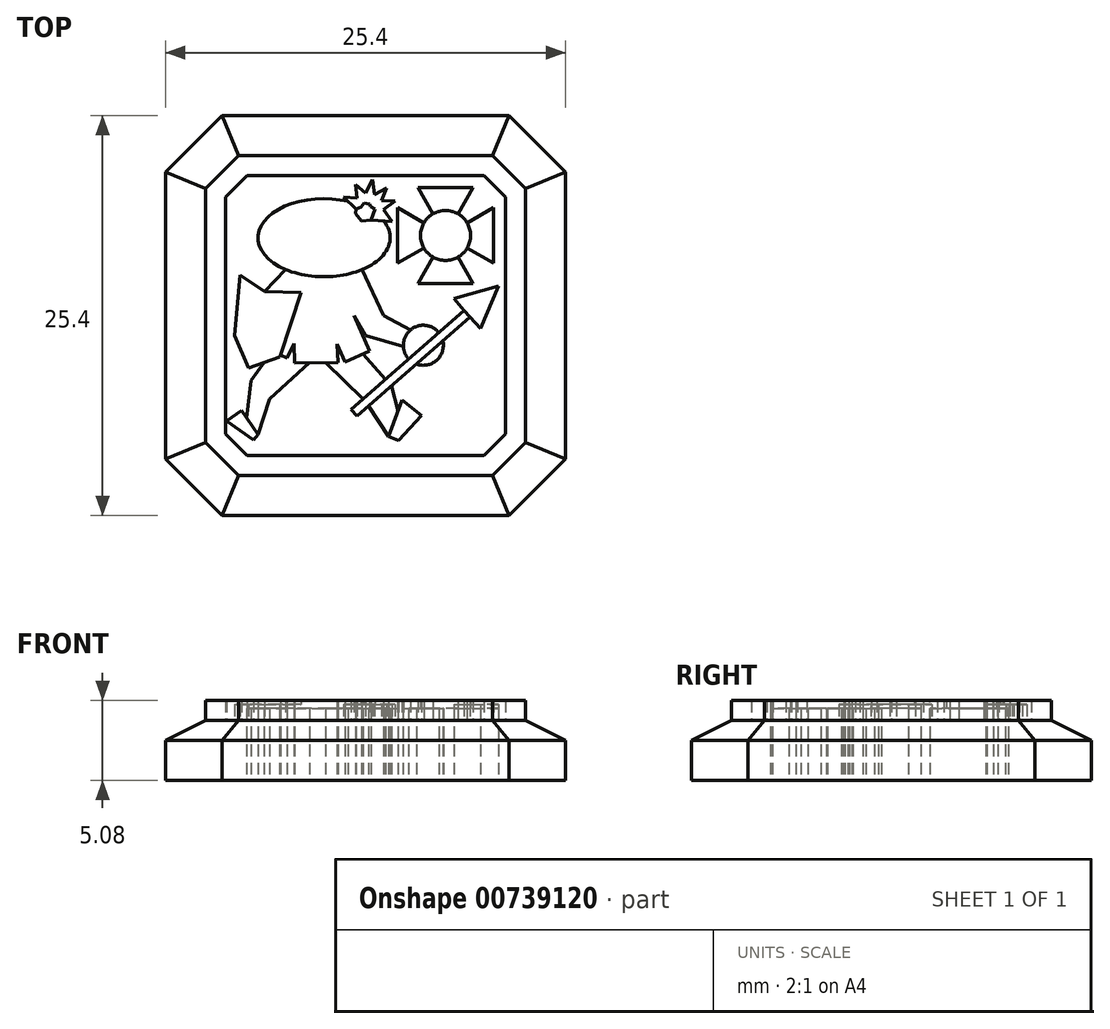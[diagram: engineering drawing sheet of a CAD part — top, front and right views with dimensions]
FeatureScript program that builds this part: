
annotation { "Feature Type Name" : "Feature", "Feature Type Description" : "" }
export const myFeature = defineFeature(function(context is Context, id is Id, definition is map)
    precondition{}
    {
        {
            var Q0;
            Q0=qCreatedBy(makeId("Top.planeOp"),FACE);
            var sketch = newSketch(context, id + "F0", { "sketchPlane" : qUnion([Q0])});
            skLineSegment(sketch, "E0", {"start": v(0, 34.78) * mm, "end": v(0, -32.67) * mm, "construction": true});
            skLineSegment(sketch, "E1", {"start": v(-47.17, 0) * mm, "end": v(41.3, 0) * mm});
            skLineSegment(sketch, "E2", {"start": v(0, 12.7) * mm, "end": v(-9.1, 12.7) * mm});
            skLineSegment(sketch, "E3", {"start": v(-9.1, 12.7) * mm, "end": v(-12.7, 9.1) * mm});
            skLineSegment(sketch, "E4", {"start": v(-12.7, 9.1) * mm, "end": v(-12.7, 0) * mm});
            skLineSegment(sketch, "E5.MirrorCS", {"start": v(0, 12.7) * mm, "end": v(9.1, 12.7) * mm});
            skLineSegment(sketch, "E6.MirrorCS", {"start": v(9.1, 12.7) * mm, "end": v(12.7, 9.1) * mm});
            skLineSegment(sketch, "E7.MirrorCS", {"start": v(12.7, 9.1) * mm, "end": v(12.7, 0) * mm});
            skLineSegment(sketch, "E8.MirrorCS", {"start": v(12.7, -9.1) * mm, "end": v(12.7, 0) * mm});
            skLineSegment(sketch, "E9.MirrorCS", {"start": v(9.1, -12.7) * mm, "end": v(12.7, -9.1) * mm});
            skLineSegment(sketch, "E10.MirrorCS", {"start": v(0, -12.7) * mm, "end": v(9.1, -12.7) * mm});
            skLineSegment(sketch, "E11.MirrorCS", {"start": v(0, -12.7) * mm, "end": v(-9.1, -12.7) * mm});
            skLineSegment(sketch, "E12.MirrorCS", {"start": v(-9.1, -12.7) * mm, "end": v(-12.7, -9.1) * mm});
            skLineSegment(sketch, "E13.MirrorCS", {"start": v(-12.7, -9.1) * mm, "end": v(-12.7, 0) * mm});
            skSolve(sketch);
        }
        {
            var Q0;
            Q0=makeQuery(id+"F0.imprint","IMPRINT",FACE,{"disambiguationData":[TD([[makeQuery(id+"F0.imprint","IMPRINT",EDGE,{"derivedFrom":sQuery(id+"F0.wireOp",EDGE,"E2")}),1.0]])]});
            var Q1;
            {var subQ0=sQuery(id+"F0.wireOp",EDGE,"E8.MirrorCS");Q1=makeQuery(id+"F0.imprint","IMPRINT",FACE,{"disambiguationData":[TD([[makeQuery(id+"F0.imprint","IMPRINT",EDGE,{"derivedFrom":subQ0}),1.0]])]});}
            extrude(context, id + "F1", {"entities" : qUnion([Q0, Q1]), "depth" : 3.8 * mm, "offsetDistance" : 25.4 * mm});
        }
        {
            var Q0;
            Q0=makeQuery(id+"F1.opExtrude","CAP_EDGE",EDGE,{"disambiguationData":[OSD([sQuery(id+"F0.wireOp",EDGE,"E10.MirrorCS"),sQuery(id+"F0.wireOp",EDGE,"E11.MirrorCS")])],"isStart":false});
            var Q1;
            Q1=makeQuery(id+"F1.opExtrude","CAP_EDGE",EDGE,{"disambiguationData":[OSD([sQuery(id+"F0.wireOp",EDGE,"E4"),sQuery(id+"F0.wireOp",EDGE,"E13.MirrorCS")])],"isStart":false});
            var Q2;
            Q2=makeQuery(id+"F1.opExtrude","CAP_EDGE",EDGE,{"disambiguationData":[OSD([sQuery(id+"F0.wireOp",EDGE,"E2"),sQuery(id+"F0.wireOp",EDGE,"E5.MirrorCS")])],"isStart":false});
            var Q3;
            Q3=makeQuery(id+"F1.opExtrude","CAP_EDGE",EDGE,{"disambiguationData":[OSD([sQuery(id+"F0.wireOp",EDGE,"E7.MirrorCS"),sQuery(id+"F0.wireOp",EDGE,"E8.MirrorCS")])],"isStart":false});
            var Q4;
            Q4=makeQuery(id+"F1.opExtrude","CAP_EDGE",EDGE,{"disambiguationData":[OSD([sQuery(id+"F0.wireOp",EDGE,"E6.MirrorCS")])],"isStart":false});
            var Q5;
            Q5=makeQuery(id+"F1.opExtrude","CAP_EDGE",EDGE,{"disambiguationData":[OSD([sQuery(id+"F0.wireOp",EDGE,"E3")])],"isStart":false});
            var Q6;
            Q6=makeQuery(id+"F1.opExtrude","CAP_EDGE",EDGE,{"disambiguationData":[OSD([sQuery(id+"F0.wireOp",EDGE,"E9.MirrorCS")])],"isStart":false});
            var Q7;
            Q7=makeQuery(id+"F1.opExtrude","CAP_EDGE",EDGE,{"disambiguationData":[OSD([sQuery(id+"F0.wireOp",EDGE,"E12.MirrorCS")])],"isStart":false});
            chamfer(context, id + "F2", {"entities" : qUnion([Q0, Q1, Q2, Q3, Q4, Q5, Q6, Q7]), "chamferType" : ChamferType.TWO_OFFSETS, "width1" : 1.27 * mm, "oppositeDirection" : false, "width2" : 2.54 * mm, "tangentPropagation" : true});
        }
        {
            var Q0;
            Q0=qCreatedBy(makeId("Top.planeOp"),FACE);
            var sketch = newSketch(context, id + "F3", { "sketchPlane" : qUnion([Q0])});
            skLineSegment(sketch, "E14", {"start": v(-10.16, 8.06) * mm, "end": v(-8.06, 10.16) * mm});
            skLineSegment(sketch, "E15", {"start": v(-8.06, 10.16) * mm, "end": v(0, 10.16) * mm});
            skLineSegment(sketch, "E16", {"start": v(-10.16, 8.06) * mm, "end": v(-10.16, 0) * mm});
            skLineSegment(sketch, "E17", {"start": v(-15.43, 0) * mm, "end": v(15.43, 0) * mm, "construction": true});
            skLineSegment(sketch, "E18", {"start": v(0, 15.6) * mm, "end": v(0, -14.81) * mm, "construction": true});
            skLineSegment(sketch, "E19.MirrorCS", {"start": v(8.06, 10.16) * mm, "end": v(0, 10.16) * mm});
            skLineSegment(sketch, "E20.MirrorCS", {"start": v(10.16, 8.06) * mm, "end": v(8.06, 10.16) * mm});
            skLineSegment(sketch, "E21.MirrorCS", {"start": v(10.16, 8.06) * mm, "end": v(10.16, 0) * mm});
            skLineSegment(sketch, "E22.MirrorCS", {"start": v(-10.16, -8.06) * mm, "end": v(-10.16, 0) * mm});
            skLineSegment(sketch, "E23.MirrorCS", {"start": v(-10.16, -8.06) * mm, "end": v(-8.06, -10.16) * mm});
            skLineSegment(sketch, "E24.MirrorCS", {"start": v(-8.06, -10.16) * mm, "end": v(0, -10.16) * mm});
            skLineSegment(sketch, "E25.MirrorCS", {"start": v(8.06, -10.16) * mm, "end": v(0, -10.16) * mm});
            skLineSegment(sketch, "E26.MirrorCS", {"start": v(10.16, -8.06) * mm, "end": v(8.06, -10.16) * mm});
            skLineSegment(sketch, "E27.MirrorCS", {"start": v(10.16, -8.06) * mm, "end": v(10.16, 0) * mm});
            skLineSegment(sketch, "E28", {"start": v(0, 8.9) * mm, "end": v(-7.53, 8.9) * mm});
            skLineSegment(sketch, "E29", {"start": v(-8.89, 7.53) * mm, "end": v(-8.89, 0) * mm});
            skLineSegment(sketch, "E30", {"start": v(-8.89, 7.53) * mm, "end": v(-7.53, 8.9) * mm});
            skLineSegment(sketch, "E31.MirrorCS", {"start": v(0, 8.9) * mm, "end": v(7.53, 8.9) * mm});
            skLineSegment(sketch, "E32.MirrorCS", {"start": v(8.89, 7.53) * mm, "end": v(7.53, 8.9) * mm});
            skLineSegment(sketch, "E33.MirrorCS", {"start": v(8.89, 7.53) * mm, "end": v(8.89, 0) * mm});
            skLineSegment(sketch, "E34.MirrorCS", {"start": v(-8.89, -7.53) * mm, "end": v(-8.89, 0) * mm});
            skLineSegment(sketch, "E35.MirrorCS", {"start": v(-8.89, -7.53) * mm, "end": v(-7.53, -8.9) * mm});
            skLineSegment(sketch, "E36.MirrorCS", {"start": v(0, -8.9) * mm, "end": v(-7.53, -8.9) * mm});
            skLineSegment(sketch, "E37.MirrorCS", {"start": v(0, -8.9) * mm, "end": v(7.53, -8.9) * mm});
            skLineSegment(sketch, "E38.MirrorCS", {"start": v(8.89, -7.53) * mm, "end": v(7.53, -8.9) * mm});
            skLineSegment(sketch, "E39.MirrorCS", {"start": v(8.89, -7.53) * mm, "end": v(8.89, 0) * mm});
            skSolve(sketch);
        }
        {
            var Q0;
            Q0=makeQuery(id+"F3.imprint","IMPRINT",FACE,{"disambiguationData":[TD([[makeQuery(id+"F3.imprint","IMPRINT",EDGE,{"derivedFrom":sQuery(id+"F3.wireOp",EDGE,"E14")}),-1.0]])]});
            extrude(context, id + "F4", {"entities" : qUnion([Q0]), "operationType" : NewBodyOperationType.ADD, "depth" : 5.08 * mm, "offsetDistance" : 25.4 * mm});
        }
        {
            var Q0;
            Q0=qCreatedBy(makeId("Top.planeOp"),FACE);
            var sketch = newSketch(context, id + "F5", { "sketchPlane" : qUnion([Q0])});
            skLineSegment(sketch, "E40", {"start": v(5.08, 14.2) * mm, "end": v(5.08, -5.22) * mm, "construction": true});
            skLineSegment(sketch, "E41", {"start": v(-0.61, 5.08) * mm, "end": v(13.42, 5.08) * mm, "construction": true});
            skCircle(sketch, "E42", {"center": v(5.08, 5.08) * mm, "radius": 1.59 * mm});
            skLineSegment(sketch, "E43", {"start": v(5.08, 5.08) * mm, "end": v(7.72, 7.72) * mm, "construction": true});
            skLineSegment(sketch, "E44", {"start": v(5.87, 6.45) * mm, "end": v(6.84, 8.13) * mm});
            skLineSegment(sketch, "E45", {"start": v(6.84, 8.13) * mm, "end": v(5.08, 8.13) * mm});
            skLineSegment(sketch, "E46.MirrorCS", {"start": v(3.32, 8.13) * mm, "end": v(5.08, 8.13) * mm});
            skLineSegment(sketch, "E47.MirrorCS", {"start": v(4.29, 6.45) * mm, "end": v(3.32, 8.13) * mm});
            skLineSegment(sketch, "E48.MirrorCS", {"start": v(6.45, 5.87) * mm, "end": v(8.13, 6.84) * mm});
            skLineSegment(sketch, "E49.MirrorCS", {"start": v(8.13, 6.84) * mm, "end": v(8.13, 5.08) * mm});
            skLineSegment(sketch, "E50.MirrorCS", {"start": v(8.13, 3.32) * mm, "end": v(8.13, 5.08) * mm});
            skLineSegment(sketch, "E51.MirrorCS", {"start": v(6.45, 4.29) * mm, "end": v(8.13, 3.32) * mm});
            skLineSegment(sketch, "E52.MirrorCS", {"start": v(5.87, 3.7) * mm, "end": v(6.84, 2.03) * mm});
            skLineSegment(sketch, "E53.MirrorCS", {"start": v(6.84, 2.03) * mm, "end": v(5.08, 2.03) * mm});
            skLineSegment(sketch, "E54.MirrorCS", {"start": v(3.32, 2.03) * mm, "end": v(5.08, 2.03) * mm});
            skLineSegment(sketch, "E55.MirrorCS", {"start": v(4.29, 3.7) * mm, "end": v(3.32, 2.03) * mm});
            skLineSegment(sketch, "E56.MirrorCS", {"start": v(3.7, 4.29) * mm, "end": v(2.03, 3.32) * mm});
            skLineSegment(sketch, "E57.MirrorCS", {"start": v(2.03, 3.32) * mm, "end": v(2.03, 5.08) * mm});
            skLineSegment(sketch, "E58.MirrorCS", {"start": v(2.03, 6.84) * mm, "end": v(2.03, 5.08) * mm});
            skLineSegment(sketch, "E59.MirrorCS", {"start": v(3.7, 5.87) * mm, "end": v(2.03, 6.84) * mm});
            skSolve(sketch);
        }
        {
            var Q0;
            {var subQ0=sQuery(id+"F5.wireOp",EDGE,"E44");Q0=makeQuery(id+"F5.imprint","IMPRINT",FACE,{"disambiguationData":[TD([[makeQuery(id+"F5.imprint","IMPRINT",EDGE,{"derivedFrom":subQ0}),1.0]])]});}
            var Q1;
            {var subQ0=sQuery(id+"F5.wireOp",EDGE,"E56.MirrorCS");Q1=makeQuery(id+"F5.imprint","IMPRINT",FACE,{"disambiguationData":[TD([[makeQuery(id+"F5.imprint","IMPRINT",EDGE,{"derivedFrom":subQ0}),-1.0]])]});}
            var Q2;
            {var subQ0=sQuery(id+"F5.wireOp",EDGE,"E52.MirrorCS");Q2=makeQuery(id+"F5.imprint","IMPRINT",FACE,{"disambiguationData":[TD([[makeQuery(id+"F5.imprint","IMPRINT",EDGE,{"derivedFrom":subQ0}),-1.0]])]});}
            var Q3;
            {var subQ0=sQuery(id+"F5.wireOp",EDGE,"E48.MirrorCS");Q3=makeQuery(id+"F5.imprint","IMPRINT",FACE,{"disambiguationData":[TD([[makeQuery(id+"F5.imprint","IMPRINT",EDGE,{"derivedFrom":subQ0}),-1.0]])]});}
            extrude(context, id + "F6", {"entities" : qUnion([Q0, Q1, Q2, Q3]), "operationType" : NewBodyOperationType.ADD, "depth" : 5.08 * mm, "offsetDistance" : 25.4 * mm});
        }
        {
            var Q0;
            {var subQ0=sQuery(id+"F5.wireOp",EDGE,"E42");var subQ4=makeQuery(id+"F5.imprint","INTERSECT",VERTEX,{"derivedFrom":[subQ0,sQuery(id+"F5.wireOp",EDGE,"E44")]});Q0=makeQuery(id+"F5.imprint","IMPRINT",FACE,{"disambiguationData":[TD([[makeQuery(id+"F5.imprint","IMPRINT",EDGE,{"disambiguationData":[TD([[subQ4,1.0]])],"derivedFrom":subQ0}),1.0]])]});}
            extrude(context, id + "F7", {"entities" : qUnion([Q0]), "operationType" : NewBodyOperationType.ADD, "depth" : 4.57 * mm, "offsetDistance" : 25.4 * mm});
        }
        {
            var Q0;
            Q0=qCreatedBy(makeId("Top.planeOp"),FACE);
            var sketch = newSketch(context, id + "F8", { "sketchPlane" : qUnion([Q0])});
            skEllipse(sketch, "E60", {"center": v(-2.64, 4.94) * mm, "majorRadius": 4.2 * mm, "minorRadius": 2.48 * mm, "majorAxis": v(-1, 0)});
            skLineSegment(sketch, "E61", {"start": v(-5.07, 2.91) * mm, "end": v(-6.43, 1.53) * mm});
            skLineSegment(sketch, "E62", {"start": v(-0.2, 2.91) * mm, "end": v(1.13, 0) * mm});
            skLineSegment(sketch, "E63", {"start": v(1.13, 0) * mm, "end": v(3.89, -1.49) * mm});
            skLineSegment(sketch, "E64", {"start": v(3.89, -1.49) * mm, "end": v(3.45, -2.3) * mm});
            skLineSegment(sketch, "E65", {"start": v(3.45, -2.3) * mm, "end": v(0, -1.26) * mm});
            skLineSegment(sketch, "E66", {"start": v(0, -1.26) * mm, "end": v(-0.73, 0) * mm});
            skCircle(sketch, "E67", {"center": v(3.67, -1.9) * mm, "radius": 1.27 * mm});
            skLineSegment(sketch, "E68", {"start": v(-0.92, -5.98) * mm, "end": v(6.27, 0.33) * mm});
            skLineSegment(sketch, "E69", {"start": v(7.82, 1.7) * mm, "end": v(5.62, 1.07) * mm});
            skLineSegment(sketch, "E70", {"start": v(5.62, 1.07) * mm, "end": v(7.29, -0.84) * mm});
            skLineSegment(sketch, "E71", {"start": v(-0.92, -5.98) * mm, "end": v(-0.55, -6.4) * mm});
            skLineSegment(sketch, "E72", {"start": v(-0.55, -6.4) * mm, "end": v(6.64, -0.1) * mm});
            skLineSegment(sketch, "E73", {"start": v(7.82, 1.7) * mm, "end": v(8.45, 1.87) * mm});
            skLineSegment(sketch, "E74", {"start": v(-0.73, -6.19) * mm, "end": v(9.14, 2.47) * mm, "construction": true});
            skLineSegment(sketch, "E75.MirrorCS", {"start": v(8.2, 1.27) * mm, "end": v(7.29, -0.84) * mm});
            skLineSegment(sketch, "E76.MirrorCS", {"start": v(8.2, 1.27) * mm, "end": v(8.45, 1.87) * mm});
            skLineSegment(sketch, "E77", {"start": v(-7.97, 2.57) * mm, "end": v(-6.43, 1.53) * mm});
            skLineSegment(sketch, "E78", {"start": v(-5.45, -2.65) * mm, "end": v(-7.43, -3.32) * mm});
            skLineSegment(sketch, "E79", {"start": v(-7.43, -3.32) * mm, "end": v(-8.33, -1.29) * mm});
            skLineSegment(sketch, "E80", {"start": v(-8.33, -1.29) * mm, "end": v(-7.97, 2.57) * mm});
            skLineSegment(sketch, "E81", {"start": v(-6.43, 1.53) * mm, "end": v(-4.1, 1.45) * mm});
            skLineSegment(sketch, "E82", {"start": v(-4.1, 1.45) * mm, "end": v(-5.45, -2.65) * mm});
            skLineSegment(sketch, "E83", {"start": v(-0.73, 0) * mm, "end": v(0.25, -2.27) * mm});
            skLineSegment(sketch, "E84", {"start": v(0.25, -2.27) * mm, "end": v(-1.31, -2.95) * mm});
            skLineSegment(sketch, "E85", {"start": v(-1.31, -2.95) * mm, "end": v(-1.8, -1.82) * mm});
            skLineSegment(sketch, "E86", {"start": v(-1.8, -1.82) * mm, "end": v(-1.74, -2.98) * mm});
            skLineSegment(sketch, "E87", {"start": v(-1.74, -2.98) * mm, "end": v(-4.5, -3.01) * mm});
            skLineSegment(sketch, "E88", {"start": v(-4.5, -3.01) * mm, "end": v(-4.55, -1.8) * mm});
            skLineSegment(sketch, "E89", {"start": v(-4.55, -1.8) * mm, "end": v(-4.98, -2.71) * mm});
            skLineSegment(sketch, "E90", {"start": v(-4.98, -2.71) * mm, "end": v(-5.4, -2.5) * mm});
            skLineSegment(sketch, "E91", {"start": v(-0.15, -2.44) * mm, "end": v(1.27, -4.06) * mm});
            skLineSegment(sketch, "E92", {"start": v(1.65, -4.47) * mm, "end": v(2.31, -7.13) * mm});
            skLineSegment(sketch, "E93", {"start": v(2.31, -7.13) * mm, "end": v(1.45, -7.69) * mm});
            skLineSegment(sketch, "E94", {"start": v(1.45, -7.69) * mm, "end": v(0.19, -5.76) * mm});
            skLineSegment(sketch, "E95", {"start": v(-2.54, -3) * mm, "end": v(-0.1, -5.38) * mm});
            skLineSegment(sketch, "E96", {"start": v(-3.57, -3) * mm, "end": v(-6.09, -5.3) * mm});
            skLineSegment(sketch, "E97", {"start": v(-6.09, -5.3) * mm, "end": v(-6.83, -7.57) * mm});
            skLineSegment(sketch, "E98", {"start": v(-6.83, -7.57) * mm, "end": v(-7.68, -7.41) * mm});
            skLineSegment(sketch, "E99", {"start": v(-7.68, -7.41) * mm, "end": v(-7.28, -4.14) * mm});
            skLineSegment(sketch, "E100", {"start": v(-7.28, -4.14) * mm, "end": v(-6.44, -2.99) * mm});
            skLineSegment(sketch, "E101", {"start": v(1.45, -7.69) * mm, "end": v(2.31, -5.37) * mm});
            skLineSegment(sketch, "E102", {"start": v(2.31, -5.37) * mm, "end": v(3.55, -6.35) * mm});
            skLineSegment(sketch, "E103", {"start": v(3.55, -6.35) * mm, "end": v(2.1, -7.94) * mm});
            skLineSegment(sketch, "E104", {"start": v(2.1, -7.94) * mm, "end": v(1.45, -7.69) * mm});
            skLineSegment(sketch, "E105", {"start": v(-6.83, -7.57) * mm, "end": v(-7.88, -6.05) * mm});
            skLineSegment(sketch, "E106", {"start": v(-7.88, -6.05) * mm, "end": v(-8.81, -6.7) * mm});
            skLineSegment(sketch, "E107", {"start": v(-8.81, -6.7) * mm, "end": v(-7.11, -7.9) * mm});
            skLineSegment(sketch, "E108", {"start": v(-7.11, -7.9) * mm, "end": v(-6.83, -7.57) * mm});
            skLineSegment(sketch, "E109", {"start": v(-0.63, 6.47) * mm, "end": v(-0.24, 5.99) * mm});
            skLineSegment(sketch, "E110", {"start": v(-0.24, 5.99) * mm, "end": v(0.34, 6.06) * mm});
            skLineSegment(sketch, "E111", {"start": v(0.34, 6.06) * mm, "end": v(0.6, 6.76) * mm});
            skLineSegment(sketch, "E112", {"start": v(0.6, 6.76) * mm, "end": v(0.3, 6.9) * mm});
            skLineSegment(sketch, "E113", {"start": v(0.3, 6.9) * mm, "end": v(0.27, 7.09) * mm});
            skLineSegment(sketch, "E114", {"start": v(0.27, 7.09) * mm, "end": v(-0.11, 7.14) * mm});
            skLineSegment(sketch, "E115", {"start": v(-0.11, 7.14) * mm, "end": v(-0.3, 6.87) * mm});
            skLineSegment(sketch, "E116", {"start": v(-0.3, 6.87) * mm, "end": v(-0.6, 6.75) * mm});
            skLineSegment(sketch, "E117", {"start": v(-0.6, 6.75) * mm, "end": v(-0.63, 6.47) * mm});
            skLineSegment(sketch, "E118", {"start": v(-0.6, 6.75) * mm, "end": v(-1.4, 7.53) * mm});
            skLineSegment(sketch, "E119", {"start": v(-1.4, 7.53) * mm, "end": v(-0.55, 7.45) * mm});
            skLineSegment(sketch, "E120", {"start": v(-0.55, 7.45) * mm, "end": v(-0.65, 8.3) * mm});
            skLineSegment(sketch, "E121", {"start": v(-0.65, 8.3) * mm, "end": v(0, 7.79) * mm});
            skLineSegment(sketch, "E122", {"start": v(0, 7.79) * mm, "end": v(0.45, 8.62) * mm});
            skLineSegment(sketch, "E123", {"start": v(0.45, 8.62) * mm, "end": v(0.58, 7.69) * mm});
            skLineSegment(sketch, "E124", {"start": v(0.58, 7.69) * mm, "end": v(1.33, 8.1) * mm});
            skLineSegment(sketch, "E125", {"start": v(1.33, 8.1) * mm, "end": v(1, 7.3) * mm});
            skLineSegment(sketch, "E126", {"start": v(1, 7.3) * mm, "end": v(1.88, 7.26) * mm});
            skLineSegment(sketch, "E127", {"start": v(1.88, 7.26) * mm, "end": v(1.13, 6.72) * mm});
            skLineSegment(sketch, "E128", {"start": v(1.13, 6.72) * mm, "end": v(1.67, 5.97) * mm});
            skLineSegment(sketch, "E129", {"start": v(1.67, 5.97) * mm, "end": v(1.67, 5.97) * mm});
            skLineSegment(sketch, "E130", {"start": v(1.67, 5.97) * mm, "end": v(0.34, 6.06) * mm});
            skSolve(sketch);
        }
        {
            var Q0;
            {var subQ0=sQuery(id+"F8.wireOp",EDGE,"E112");Q0=makeQuery(id+"F8.imprint","IMPRINT",FACE,{"disambiguationData":[TD([[makeQuery(id+"F8.imprint","IMPRINT",EDGE,{"derivedFrom":subQ0}),1.0]])]});}
            var Q1;
            Q1=makeQuery(id+"F8.imprint","IMPRINT",FACE,{"disambiguationData":[TD([[makeQuery(id+"F8.imprint","IMPRINT",EDGE,{"derivedFrom":sQuery(id+"F8.wireOp",EDGE,"E109")}),1.0]])]});
            var Q2;
            {var subQ7=sQuery(id+"F8.wireOp",EDGE,"E61");Q2=makeQuery(id+"F8.imprint","IMPRINT",FACE,{"disambiguationData":[TD([[makeQuery(id+"F8.imprint","IMPRINT",EDGE,{"derivedFrom":subQ7}),1.0]])]});}
            var Q3;
            {var subQ0=sQuery(id+"F8.wireOp",EDGE,"E68");var subQ1=sQuery(id+"F8.wireOp",EDGE,"E67");var subQ2=makeQuery(id+"F8.imprint","INTERSECT",VERTEX,{"disambiguationData":[OD(0.0)],"derivedFrom":[subQ1,subQ0]});Q3=makeQuery(id+"F8.imprint","IMPRINT",FACE,{"disambiguationData":[TD([[makeQuery(id+"F8.imprint","IMPRINT",EDGE,{"disambiguationData":[TD([[subQ2,1.0]])],"derivedFrom":subQ1}),-1.0]])]});}
            var Q4;
            {var subQ8=sQuery(id+"F8.wireOp",EDGE,"E71");Q4=makeQuery(id+"F8.imprint","IMPRINT",FACE,{"disambiguationData":[TD([[makeQuery(id+"F8.imprint","IMPRINT",EDGE,{"derivedFrom":subQ8}),1.0]])]});}
            var Q5;
            {var subQ5=sQuery(id+"F8.wireOp",EDGE,"E65");var subQ6=sQuery(id+"F8.wireOp",EDGE,"E64");var subQ7=makeQuery(id+"F8.imprint","INTERSECT",VERTEX,{"derivedFrom":[subQ6,subQ5]});Q5=makeQuery(id+"F8.imprint","IMPRINT",FACE,{"disambiguationData":[TD([[makeQuery(id+"F8.imprint","IMPRINT",EDGE,{"disambiguationData":[TD([[subQ7,1.0]])],"derivedFrom":subQ6}),1.0]])]});}
            var Q6;
            {var subQ0=sQuery(id+"F8.wireOp",EDGE,"E65");var subQ1=sQuery(id+"F8.wireOp",EDGE,"E64");var subQ2=makeQuery(id+"F8.imprint","INTERSECT",VERTEX,{"derivedFrom":[subQ1,subQ0]});Q6=makeQuery(id+"F8.imprint","IMPRINT",FACE,{"disambiguationData":[TD([[makeQuery(id+"F8.imprint","IMPRINT",EDGE,{"disambiguationData":[TD([[subQ2,1.0]])],"derivedFrom":subQ1}),-1.0]])]});}
            var Q7;
            {var subQ1=sQuery(id+"F8.wireOp",EDGE,"E93");Q7=makeQuery(id+"F8.imprint","IMPRINT",FACE,{"disambiguationData":[TD([[makeQuery(id+"F8.imprint","IMPRINT",EDGE,{"derivedFrom":subQ1}),1.0]])]});}
            var Q8;
            {var subQ0=sQuery(id+"F8.wireOp",EDGE,"E93");Q8=makeQuery(id+"F8.imprint","IMPRINT",FACE,{"disambiguationData":[TD([[makeQuery(id+"F8.imprint","IMPRINT",EDGE,{"derivedFrom":subQ0}),-1.0]])]});}
            var Q9;
            {var subQ1=sQuery(id+"F8.wireOp",EDGE,"E98");Q9=makeQuery(id+"F8.imprint","IMPRINT",FACE,{"disambiguationData":[TD([[makeQuery(id+"F8.imprint","IMPRINT",EDGE,{"derivedFrom":subQ1}),1.0]])]});}
            var Q10;
            {var subQ0=sQuery(id+"F8.wireOp",EDGE,"E98");Q10=makeQuery(id+"F8.imprint","IMPRINT",FACE,{"disambiguationData":[TD([[makeQuery(id+"F8.imprint","IMPRINT",EDGE,{"derivedFrom":subQ0}),-1.0]])]});}
            extrude(context, id + "F9", {"entities" : qUnion([Q0, Q1, Q2, Q3, Q4, Q5, Q6, Q7, Q8, Q9, Q10]), "operationType" : NewBodyOperationType.ADD, "depth" : 5.08 * mm, "offsetDistance" : 25.4 * mm});
        }
        {
            var Q0;
            {var subQ5=sQuery(id+"F8.wireOp",EDGE,"E116");Q0=makeQuery(id+"F8.imprint","IMPRINT",FACE,{"disambiguationData":[TD([[makeQuery(id+"F8.imprint","IMPRINT",EDGE,{"derivedFrom":subQ5}),-1.0]])]});}
            var Q1;
            {var subQ11=sQuery(id+"F8.wireOp",EDGE,"E112");Q1=makeQuery(id+"F8.imprint","IMPRINT",FACE,{"disambiguationData":[TD([[makeQuery(id+"F8.imprint","IMPRINT",EDGE,{"derivedFrom":subQ11}),-1.0]])]});}
            var Q2;
            {var subQ0=sQuery(id+"F8.wireOp",EDGE,"E130");var subQ1=sQuery(id+"F8.wireOp",EDGE,"E60");var subQ2=makeQuery(id+"F8.imprint","INTERSECT",VERTEX,{"derivedFrom":[subQ1,subQ0]});Q2=makeQuery(id+"F8.imprint","IMPRINT",FACE,{"disambiguationData":[TD([[makeQuery(id+"F8.imprint","IMPRINT",EDGE,{"disambiguationData":[TD([[subQ2,-1.0]])],"derivedFrom":subQ1}),1.0]])]});}
            var Q3;
            Q3=makeQuery(id+"F8.imprint","IMPRINT",FACE,{"disambiguationData":[TD([[makeQuery(id+"F8.imprint","IMPRINT",EDGE,{"derivedFrom":sQuery(id+"F8.wireOp",EDGE,"E77")}),-1.0]])]});
            var Q4;
            {var subQ4=sQuery(id+"F8.wireOp",EDGE,"E69");Q4=makeQuery(id+"F8.imprint","IMPRINT",FACE,{"disambiguationData":[TD([[makeQuery(id+"F8.imprint","IMPRINT",EDGE,{"derivedFrom":subQ4}),1.0]])]});}
            extrude(context, id + "F10", {"entities" : qUnion([Q0, Q1, Q2, Q3, Q4]), "operationType" : NewBodyOperationType.ADD, "depth" : 4.83 * mm, "offsetDistance" : 25.4 * mm});
        }
        {
            var Q0;
            {var subQ6=sQuery(id+"F8.wireOp",EDGE,"E88");Q0=makeQuery(id+"F8.imprint","IMPRINT",FACE,{"disambiguationData":[TD([[makeQuery(id+"F8.imprint","IMPRINT",EDGE,{"derivedFrom":subQ6}),1.0]])]});}
            var Q1;
            {var subQ1=sQuery(id+"F8.wireOp",EDGE,"E85");Q1=makeQuery(id+"F8.imprint","IMPRINT",FACE,{"disambiguationData":[TD([[makeQuery(id+"F8.imprint","IMPRINT",EDGE,{"derivedFrom":subQ1}),1.0]])]});}
            var Q2;
            {var subQ3=sQuery(id+"F8.wireOp",EDGE,"E94");Q2=makeQuery(id+"F8.imprint","IMPRINT",FACE,{"disambiguationData":[TD([[makeQuery(id+"F8.imprint","IMPRINT",EDGE,{"derivedFrom":subQ3}),-1.0]])]});}
            var Q3;
            {var subQ0=sQuery(id+"F8.wireOp",EDGE,"E68");var subQ1=sQuery(id+"F8.wireOp",EDGE,"E65");var subQ2=makeQuery(id+"F8.imprint","INTERSECT",VERTEX,{"derivedFrom":[subQ1,subQ0]});Q3=makeQuery(id+"F8.imprint","IMPRINT",FACE,{"disambiguationData":[TD([[makeQuery(id+"F8.imprint","IMPRINT",EDGE,{"disambiguationData":[TD([[subQ2,-1.0]])],"derivedFrom":subQ1}),1.0]])]});}
            var Q4;
            {var subQ0=sQuery(id+"F8.wireOp",EDGE,"E64");var subQ1=sQuery(id+"F8.wireOp",EDGE,"E63");var subQ2=makeQuery(id+"F8.imprint","INTERSECT",VERTEX,{"derivedFrom":[subQ1,subQ0]});Q4=makeQuery(id+"F8.imprint","IMPRINT",FACE,{"disambiguationData":[TD([[makeQuery(id+"F8.imprint","IMPRINT",EDGE,{"disambiguationData":[TD([[subQ2,1.0]])],"derivedFrom":subQ1}),1.0]])]});}
            var Q5;
            {var subQ0=sQuery(id+"F8.wireOp",EDGE,"E72");var subQ1=sQuery(id+"F8.wireOp",EDGE,"E67");var subQ2=makeQuery(id+"F8.imprint","INTERSECT",VERTEX,{"disambiguationData":[OD(0.0)],"derivedFrom":[subQ1,subQ0]});Q5=makeQuery(id+"F8.imprint","IMPRINT",FACE,{"disambiguationData":[TD([[makeQuery(id+"F8.imprint","IMPRINT",EDGE,{"disambiguationData":[TD([[subQ2,1.0]])],"derivedFrom":subQ1}),1.0]])]});}
            var Q6;
            {var subQ4=sQuery(id+"F8.wireOp",EDGE,"E69");Q6=makeQuery(id+"F8.imprint","IMPRINT",FACE,{"disambiguationData":[TD([[makeQuery(id+"F8.imprint","IMPRINT",EDGE,{"derivedFrom":subQ4}),1.0]])]});}
            var Q7;
            Q7=makeQuery(id+"F8.imprint","IMPRINT",FACE,{"disambiguationData":[TD([[makeQuery(id+"F8.imprint","IMPRINT",EDGE,{"derivedFrom":sQuery(id+"F8.wireOp",EDGE,"E109")}),-1.0]])]});
            var Q8;
            {var subQ1=sQuery(id+"F8.wireOp",EDGE,"E63");var subQ7=sQuery(id+"F8.wireOp",EDGE,"E64");var subQ8=makeQuery(id+"F8.imprint","INTERSECT",VERTEX,{"derivedFrom":[subQ1,subQ7]});Q8=makeQuery(id+"F8.imprint","IMPRINT",FACE,{"disambiguationData":[TD([[makeQuery(id+"F8.imprint","IMPRINT",EDGE,{"disambiguationData":[TD([[subQ8,1.0]])],"derivedFrom":subQ1}),-1.0]])]});}
            extrude(context, id + "F11", {"entities" : qUnion([Q0, Q1, Q2, Q3, Q4, Q5, Q6, Q7, Q8]), "depth" : 4.57 * mm, "offsetDistance" : 25.4 * mm});
        }
    });
